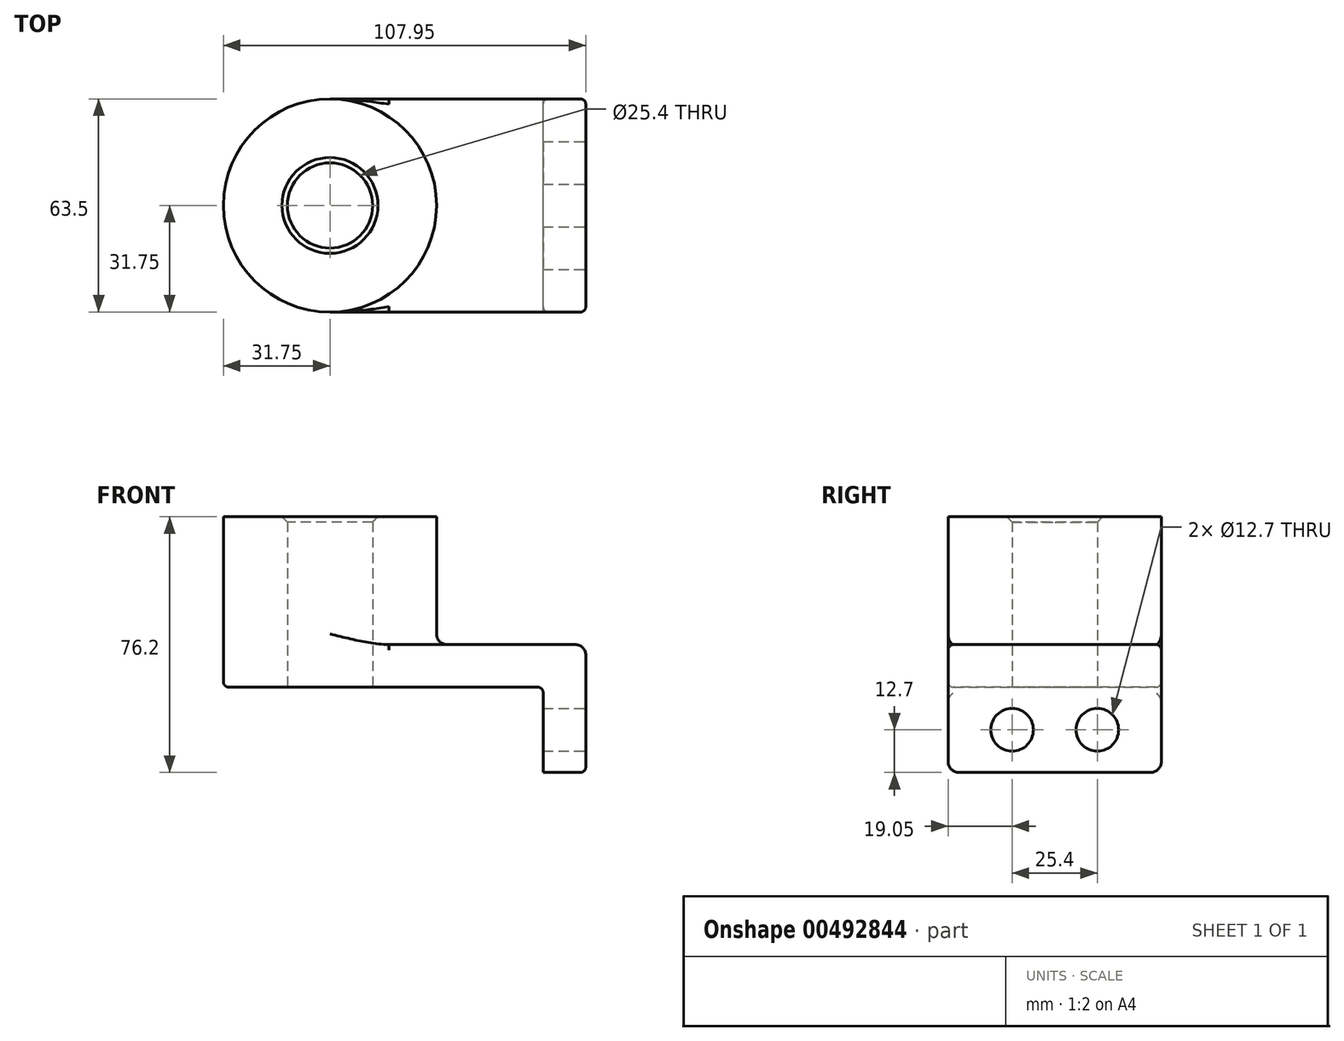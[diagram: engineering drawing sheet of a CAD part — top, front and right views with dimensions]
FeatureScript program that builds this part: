
annotation { "Feature Type Name" : "Feature", "Feature Type Description" : "" }
export const myFeature = defineFeature(function(context is Context, id is Id, definition is map)
    precondition{}
    {
        {
            var Q0;
            Q0=qCreatedBy(makeId("Top.planeOp"),FACE);
            var sketch = newSketch(context, id + "F0", { "sketchPlane" : qUnion([Q0])});
            skLineSegment(sketch, "E0.bottom", {"start": v(-38.1, 31.75) * mm, "end": v(38.1, 31.75) * mm});
            skLineSegment(sketch, "E0.top", {"start": v(-38.1, -31.75) * mm, "end": v(38.1, -31.75) * mm});
            skLineSegment(sketch, "E0.left", {"start": v(-38.1, 31.75) * mm, "end": v(-38.1, -31.75) * mm});
            skLineSegment(sketch, "E0.right", {"start": v(38.1, 31.75) * mm, "end": v(38.1, -31.75) * mm});
            skPoint(sketch, "E0.middle", {"position": v(0, 0) * mm});
            skCircle(sketch, "E1", {"center": v(-38.1, 0) * mm, "radius": 31.75 * mm});
            skCircle(sketch, "E2", {"center": v(-38.1, 0) * mm, "radius": 12.7 * mm});
            skSolve(sketch);
        }
        {
            var Q0;
            Q0 = qSketchRegion(id + "F0", true);
            extrude(context, id + "F1", {"entities" : qUnion([Q0]), "depth" : 12.7 * mm});
        }
        {
            var Q0;
            {var subQ1=sQuery(id+"F0.wireOp",EDGE,"E0.left");var subQ3=sQuery(id+"F0.wireOp",EDGE,"E2");var subQ4=makeQuery(id+"F0.imprint","INTERSECT",VERTEX,{"disambiguationData":[OD(0.0)],"derivedFrom":[subQ1,subQ3]});Q0=makeQuery(id+"F0.imprint","IMPRINT",FACE,{"disambiguationData":[TD([[makeQuery(id+"F0.imprint","IMPRINT",EDGE,{"disambiguationData":[TD([[subQ4,-1.0]])],"derivedFrom":subQ3}),-1.0]])]});}
            var Q1;
            {var subQ1=sQuery(id+"F0.wireOp",EDGE,"E0.left");var subQ3=sQuery(id+"F0.wireOp",EDGE,"E2");var subQ4=makeQuery(id+"F0.imprint","INTERSECT",VERTEX,{"disambiguationData":[OD(0.0)],"derivedFrom":[subQ1,subQ3]});Q1=makeQuery(id+"F0.imprint","IMPRINT",FACE,{"disambiguationData":[TD([[makeQuery(id+"F0.imprint","IMPRINT",EDGE,{"disambiguationData":[TD([[subQ4,1.0]])],"derivedFrom":subQ3}),-1.0]])]});}
            extrude(context, id + "F2", {"entities" : qUnion([Q0, Q1]), "operationType" : NewBodyOperationType.ADD, "depth" : 50.8 * mm});
        }
        {
            var Q0;
            Q0=makeQuery(id+"F1.opExtrude","SWEPT_FACE",FACE,{"disambiguationData":[OSD([sQuery(id+"F0.wireOp",EDGE,"E0.right")])]});
            var sketch = newSketch(context, id + "F3", { "sketchPlane" : qUnion([Q0])});
            skLineSegment(sketch, "E3.bottom", {"start": v(-31.75, 12.7) * mm, "end": v(31.75, 12.7) * mm});
            skLineSegment(sketch, "E3.top", {"start": v(-31.75, -25.4) * mm, "end": v(31.75, -25.4) * mm});
            skLineSegment(sketch, "E3.left", {"start": v(-31.75, 12.7) * mm, "end": v(-31.75, -25.4) * mm});
            skLineSegment(sketch, "E3.right", {"start": v(31.75, 12.7) * mm, "end": v(31.75, -25.4) * mm});
            skCircle(sketch, "E4", {"center": v(-12.7, -12.7) * mm, "radius": 6.35 * mm});
            skLineSegment(sketch, "E5", {"start": v(0, 0) * mm, "end": v(0, -25.4) * mm});
            skCircle(sketch, "E6.MirrorC", {"center": v(12.7, -12.7) * mm, "radius": 6.35 * mm});
            skSolve(sketch);
        }
        {
            var Q0;
            Q0 = qSketchRegion(id + "F3", true);
            extrude(context, id + "F4", {"entities" : qUnion([Q0]), "operationType" : NewBodyOperationType.ADD, "oppositeDirection" : true, "depth" : 12.7 * mm});
        }
        {
            var Q0;
            {var subQ0=sQuery(id+"F0.wireOp",EDGE,"E1");Q0=makeQuery(id+"F2.boolean.opBoolean","INTERSECT",EDGE,{"derivedFrom":[makeQuery(id+"F1.opExtrude","CAP_FACE",FACE,{"disambiguationData":[OSD([sQuery(id+"F0.wireOp",EDGE,"E0.bottom"),sQuery(id+"F0.wireOp",EDGE,"E0.top"),sQuery(id+"F0.wireOp",EDGE,"E0.right"),subQ0,sQuery(id+"F0.wireOp",EDGE,"E2")])],"isStart":false}),makeQuery(id+"F2.opExtrude","SWEPT_FACE",FACE,{"disambiguationData":[OSD([subQ0])]})]});}
            var Q1;
            Q1=makeQuery(id+"F4.opExtrude","SWEPT_EDGE",EDGE,{"disambiguationData":[OSD([sQuery(id+"F3.wireOp",EDGE,"E3.top"),sQuery(id+"F3.wireOp",EDGE,"E3.left")])]});
            var Q2;
            Q2=makeQuery(id+"F4.opExtrude","SWEPT_EDGE",EDGE,{"disambiguationData":[OSD([sQuery(id+"F3.wireOp",EDGE,"E3.top"),sQuery(id+"F3.wireOp",EDGE,"E3.right")])]});
            var Q3;
            Q3=makeQuery(id+"F1.opExtrude","CAP_EDGE",EDGE,{"disambiguationData":[OSD([sQuery(id+"F0.wireOp",EDGE,"E0.right")])],"isStart":false});
            fillet(context, id + "F5", {"entities" : qUnion([Q0, Q1, Q2, Q3]), "radius" : 3.17 * mm, "tangentPropagation" : true, "allowEdgeOverflow" : false});
        }
        {
            var Q0;
            Q0=makeQuery(id+"F1.opExtrude","CAP_EDGE",EDGE,{"disambiguationData":[OSD([sQuery(id+"F0.wireOp",EDGE,"E0.top")])],"isStart":false});
            var Q1;
            Q1=makeQuery(id+"F1.opExtrude","CAP_EDGE",EDGE,{"disambiguationData":[OSD([sQuery(id+"F0.wireOp",EDGE,"E0.top")])],"isStart":true});
            var Q2;
            Q2=makeQuery(id+"F4.boolean.opBoolean","INTERSECT",EDGE,{"derivedFrom":[makeQuery(id+"F1.opExtrude","CAP_FACE",FACE,{"disambiguationData":[OSD([sQuery(id+"F0.wireOp",EDGE,"E0.bottom"),sQuery(id+"F0.wireOp",EDGE,"E0.top"),sQuery(id+"F0.wireOp",EDGE,"E0.right"),sQuery(id+"F0.wireOp",EDGE,"E1"),sQuery(id+"F0.wireOp",EDGE,"E2")])],"isStart":true}),makeQuery(id+"F4.opExtrude","CAP_FACE",FACE,{"disambiguationData":[OSD([sQuery(id+"F3.wireOp",EDGE,"E3.bottom"),sQuery(id+"F3.wireOp",EDGE,"E3.top"),sQuery(id+"F3.wireOp",EDGE,"E3.left"),sQuery(id+"F3.wireOp",EDGE,"E3.right"),sQuery(id+"F3.wireOp",EDGE,"E4"),sQuery(id+"F3.wireOp",EDGE,"E6.MirrorC")])],"isStart":false})]});
            fillet(context, id + "F6", {"entities" : qUnion([Q0, Q1, Q2]), "radius" : 1.59 * mm, "tangentPropagation" : true, "allowEdgeOverflow" : false});
        }
        {
            var Q0;
            Q0=makeQuery(id+"F2.opExtrude","CAP_EDGE",EDGE,{"disambiguationData":[OSD([sQuery(id+"F0.wireOp",EDGE,"E2")])],"isStart":false});
            chamfer(context, id + "F7", {"entities" : qUnion([Q0]), "width" : 1.59 * mm, "tangentPropagation" : true});
        }
    });
